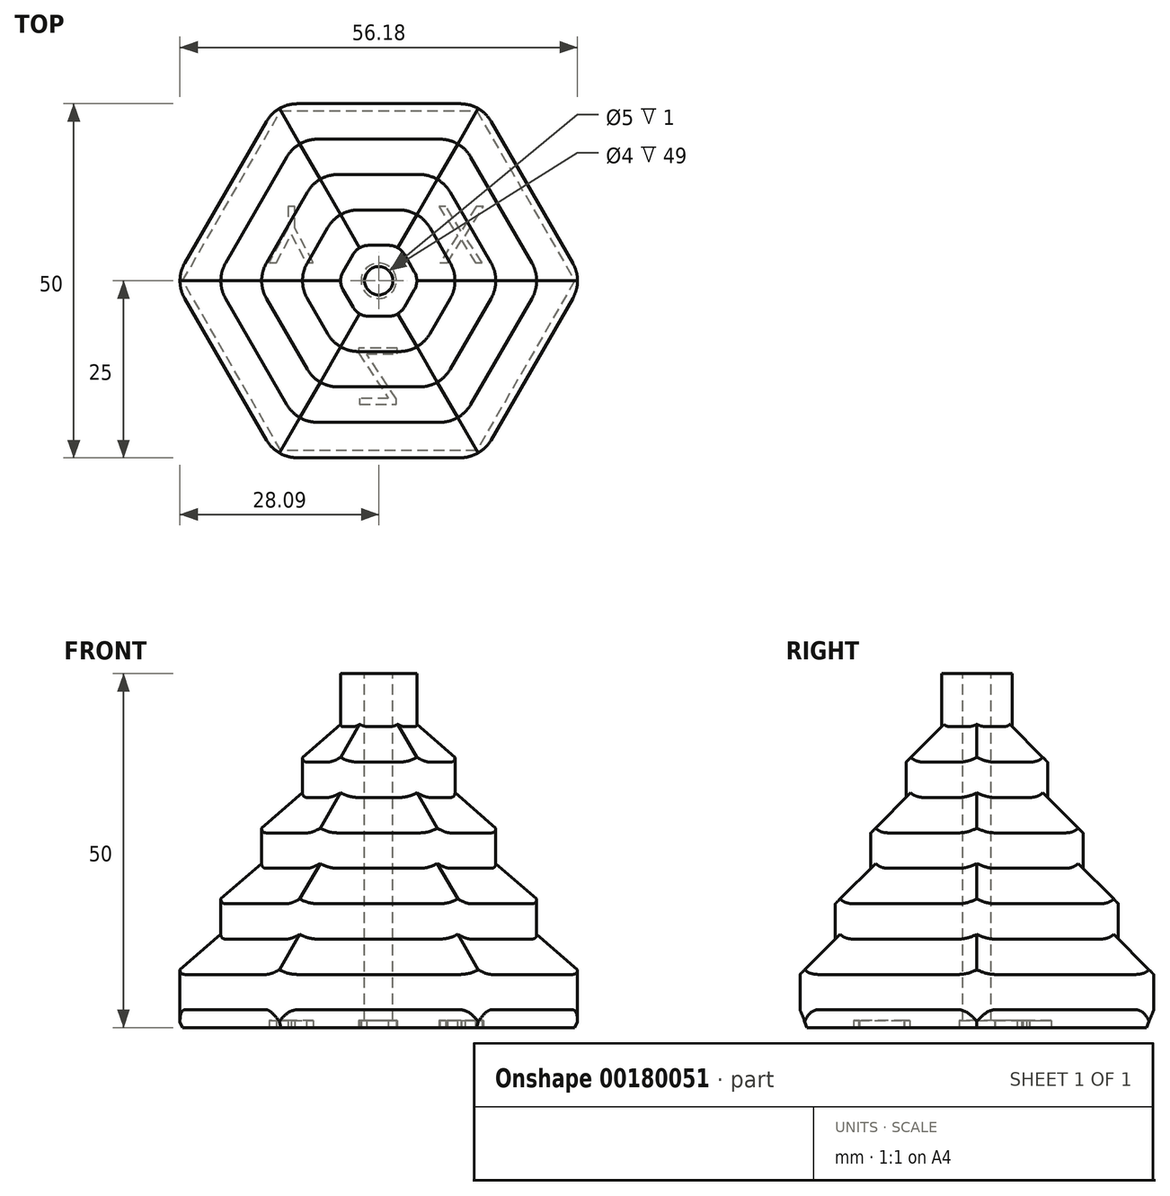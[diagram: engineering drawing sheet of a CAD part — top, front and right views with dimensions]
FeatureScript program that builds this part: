
annotation { "Feature Type Name" : "Feature", "Feature Type Description" : "" }
export const myFeature = defineFeature(function(context is Context, id is Id, definition is map)
    precondition{}
    {
        {
            var Q0;
            Q0=qCreatedBy(makeId("Top.planeOp"),FACE);
            var sketch = newSketch(context, id + "F0", { "sketchPlane" : qUnion([Q0])});
            skCircle(sketch, "E0.cCircle", {"center": v(0, 0) * mm, "radius": 25 * mm, "construction": true});
            skLineSegment(sketch, "E0.0", {"start": v(-14.43, 25) * mm, "end": v(14.43, 25) * mm});
            skLineSegment(sketch, "E0.1", {"start": v(14.43, 25) * mm, "end": v(28.87, 0) * mm});
            skLineSegment(sketch, "E0.2", {"start": v(28.87, 0) * mm, "end": v(14.43, -25) * mm});
            skLineSegment(sketch, "E0.3", {"start": v(14.43, -25) * mm, "end": v(-14.43, -25) * mm});
            skLineSegment(sketch, "E0.4", {"start": v(-14.43, -25) * mm, "end": v(-28.87, 0) * mm});
            skLineSegment(sketch, "E0.5", {"start": v(-28.87, 0) * mm, "end": v(-14.43, 25) * mm});
            skPoint(sketch, "E0.0.midPoint", {"position": v(0, 25) * mm});
            skSolve(sketch);
        }
        {
            var Q0;
            Q0 = qSketchRegion(id + "F0", true);
            extrude(context, id + "F1", {"entities" : qUnion([Q0]), "depth" : 10 * mm});
        }
        {
            var Q0;
            Q0=makeQuery(id+"F1.opExtrude","CAP_FACE",FACE,{"disambiguationData":[OSD([sQuery(id+"F0.wireOp",EDGE,"E0.0"),sQuery(id+"F0.wireOp",EDGE,"E0.1"),sQuery(id+"F0.wireOp",EDGE,"E0.2"),sQuery(id+"F0.wireOp",EDGE,"E0.3"),sQuery(id+"F0.wireOp",EDGE,"E0.4"),sQuery(id+"F0.wireOp",EDGE,"E0.5")])],"isStart":false});
            var sketch = newSketch(context, id + "F2", { "sketchPlane" : qUnion([Q0])});
            skCircle(sketch, "E1.cCircle", {"center": v(0, 0) * mm, "radius": 20 * mm, "construction": true});
            skLineSegment(sketch, "E1.0", {"start": v(-11.55, 20) * mm, "end": v(11.55, 20) * mm});
            skLineSegment(sketch, "E1.1", {"start": v(11.55, 20) * mm, "end": v(23.1, 0) * mm});
            skLineSegment(sketch, "E1.2", {"start": v(23.1, 0) * mm, "end": v(11.55, -20) * mm});
            skLineSegment(sketch, "E1.3", {"start": v(11.55, -20) * mm, "end": v(-11.55, -20) * mm});
            skLineSegment(sketch, "E1.4", {"start": v(-11.55, -20) * mm, "end": v(-23.1, 0) * mm});
            skLineSegment(sketch, "E1.5", {"start": v(-23.1, 0) * mm, "end": v(-11.55, 20) * mm});
            skPoint(sketch, "E1.0.midPoint", {"position": v(0, 20) * mm});
            skSolve(sketch);
        }
        {
            var Q0;
            Q0 = qSketchRegion(id + "F2", true);
            extrude(context, id + "F3", {"entities" : qUnion([Q0]), "operationType" : NewBodyOperationType.ADD, "depth" : 10 * mm});
        }
        {
            var Q0;
            Q0=makeQuery(id+"F3.opExtrude","CAP_FACE",FACE,{"disambiguationData":[OSD([sQuery(id+"F2.wireOp",EDGE,"E1.0"),sQuery(id+"F2.wireOp",EDGE,"E1.1"),sQuery(id+"F2.wireOp",EDGE,"E1.2"),sQuery(id+"F2.wireOp",EDGE,"E1.3"),sQuery(id+"F2.wireOp",EDGE,"E1.4"),sQuery(id+"F2.wireOp",EDGE,"E1.5")])],"isStart":false});
            var sketch = newSketch(context, id + "F4", { "sketchPlane" : qUnion([Q0])});
            skCircle(sketch, "E2.cCircle", {"center": v(0, 0) * mm, "radius": 15 * mm, "construction": true});
            skLineSegment(sketch, "E2.0", {"start": v(-8.66, 15) * mm, "end": v(8.66, 15) * mm});
            skLineSegment(sketch, "E2.1", {"start": v(8.66, 15) * mm, "end": v(17.32, 0) * mm});
            skLineSegment(sketch, "E2.2", {"start": v(17.32, 0) * mm, "end": v(8.66, -15) * mm});
            skLineSegment(sketch, "E2.3", {"start": v(8.66, -15) * mm, "end": v(-8.66, -15) * mm});
            skLineSegment(sketch, "E2.4", {"start": v(-8.66, -15) * mm, "end": v(-17.32, 0) * mm});
            skLineSegment(sketch, "E2.5", {"start": v(-17.32, 0) * mm, "end": v(-8.66, 15) * mm});
            skPoint(sketch, "E2.0.midPoint", {"position": v(0, 15) * mm});
            skSolve(sketch);
        }
        {
            var Q0;
            Q0 = qSketchRegion(id + "F4", true);
            extrude(context, id + "F5", {"entities" : qUnion([Q0]), "operationType" : NewBodyOperationType.ADD, "depth" : 10 * mm});
        }
        {
            var Q0;
            Q0=makeQuery(id+"F5.opExtrude","CAP_FACE",FACE,{"disambiguationData":[OSD([sQuery(id+"F4.wireOp",EDGE,"E2.0"),sQuery(id+"F4.wireOp",EDGE,"E2.1"),sQuery(id+"F4.wireOp",EDGE,"E2.2"),sQuery(id+"F4.wireOp",EDGE,"E2.3"),sQuery(id+"F4.wireOp",EDGE,"E2.4"),sQuery(id+"F4.wireOp",EDGE,"E2.5")])],"isStart":false});
            var sketch = newSketch(context, id + "F6", { "sketchPlane" : qUnion([Q0])});
            skCircle(sketch, "E3.cCircle", {"center": v(0, 0) * mm, "radius": 10 * mm, "construction": true});
            skLineSegment(sketch, "E3.0", {"start": v(-5.77, 10) * mm, "end": v(5.77, 10) * mm});
            skLineSegment(sketch, "E3.1", {"start": v(5.77, 10) * mm, "end": v(11.55, 0) * mm});
            skLineSegment(sketch, "E3.2", {"start": v(11.55, 0) * mm, "end": v(5.77, -10) * mm});
            skLineSegment(sketch, "E3.3", {"start": v(5.77, -10) * mm, "end": v(-5.77, -10) * mm});
            skLineSegment(sketch, "E3.4", {"start": v(-5.77, -10) * mm, "end": v(-11.55, 0) * mm});
            skLineSegment(sketch, "E3.5", {"start": v(-11.55, 0) * mm, "end": v(-5.77, 10) * mm});
            skPoint(sketch, "E3.0.midPoint", {"position": v(0, 10) * mm});
            skSolve(sketch);
        }
        {
            var Q0;
            Q0 = qSketchRegion(id + "F6", true);
            extrude(context, id + "F7", {"entities" : qUnion([Q0]), "operationType" : NewBodyOperationType.ADD, "depth" : 10 * mm});
        }
        {
            var Q0;
            Q0=makeQuery(id+"F7.opExtrude","CAP_FACE",FACE,{"disambiguationData":[OSD([sQuery(id+"F6.wireOp",EDGE,"E3.0"),sQuery(id+"F6.wireOp",EDGE,"E3.1"),sQuery(id+"F6.wireOp",EDGE,"E3.2"),sQuery(id+"F6.wireOp",EDGE,"E3.3"),sQuery(id+"F6.wireOp",EDGE,"E3.4"),sQuery(id+"F6.wireOp",EDGE,"E3.5")])],"isStart":false});
            var sketch = newSketch(context, id + "F8", { "sketchPlane" : qUnion([Q0])});
            skCircle(sketch, "E4.cCircle", {"center": v(0, 0) * mm, "radius": 5 * mm, "construction": true});
            skLineSegment(sketch, "E4.0", {"start": v(-2.89, 5) * mm, "end": v(2.89, 5) * mm});
            skLineSegment(sketch, "E4.1", {"start": v(2.89, 5) * mm, "end": v(5.77, 0) * mm});
            skLineSegment(sketch, "E4.2", {"start": v(5.77, 0) * mm, "end": v(2.89, -5) * mm});
            skLineSegment(sketch, "E4.3", {"start": v(2.89, -5) * mm, "end": v(-2.89, -5) * mm});
            skLineSegment(sketch, "E4.4", {"start": v(-2.89, -5) * mm, "end": v(-5.77, 0) * mm});
            skLineSegment(sketch, "E4.5", {"start": v(-5.77, 0) * mm, "end": v(-2.89, 5) * mm});
            skPoint(sketch, "E4.0.midPoint", {"position": v(0, 5) * mm});
            skSolve(sketch);
        }
        {
            var Q0;
            Q0 = qSketchRegion(id + "F8", true);
            extrude(context, id + "F9", {"entities" : qUnion([Q0]), "operationType" : NewBodyOperationType.ADD, "depth" : 10 * mm});
        }
        {
            var Q0;
            Q0=makeQuery(id+"F1.opExtrude","CAP_FACE",FACE,{"disambiguationData":[OSD([sQuery(id+"F0.wireOp",EDGE,"E0.0"),sQuery(id+"F0.wireOp",EDGE,"E0.1"),sQuery(id+"F0.wireOp",EDGE,"E0.2"),sQuery(id+"F0.wireOp",EDGE,"E0.3"),sQuery(id+"F0.wireOp",EDGE,"E0.4"),sQuery(id+"F0.wireOp",EDGE,"E0.5")])],"isStart":true});
            chamfer(context, id + "F10", {"entities" : qUnion([Q0]), "chamferType" : ChamferType.TWO_OFFSETS, "width1" : 1 * mm, "oppositeDirection" : false, "width2" : 2.5 * mm, "tangentPropagation" : true});
        }
        {
            var Q0;
            Q0=makeQuery(id+"F1.opExtrude","CAP_FACE",FACE,{"disambiguationData":[OSD([sQuery(id+"F0.wireOp",EDGE,"E0.0"),sQuery(id+"F0.wireOp",EDGE,"E0.1"),sQuery(id+"F0.wireOp",EDGE,"E0.2"),sQuery(id+"F0.wireOp",EDGE,"E0.3"),sQuery(id+"F0.wireOp",EDGE,"E0.4"),sQuery(id+"F0.wireOp",EDGE,"E0.5")])],"isStart":true});
            var sketch = newSketch(context, id + "F11", { "sketchPlane" : qUnion([Q0])});
            skText(sketch, "E5", { "text": "Z", "fontName": "OpenSans-Regular.ttf"});
            skText(sketch, "E6", { "text": "X", "fontName": "OpenSans-Regular.ttf"});
            skText(sketch, "E7", { "text": "Y", "fontName": "OpenSans-Regular.ttf"});
            skLineSegment(sketch, "E8", {"start": v(0, 24) * mm, "end": v(0, 0) * mm, "construction": true});
            skLineSegment(sketch, "E9", {"start": v(0, 0) * mm, "end": v(-20.78, -12) * mm, "construction": true});
            skLineSegment(sketch, "E10", {"start": v(0, 0) * mm, "end": v(20.78, -12) * mm, "construction": true});
            skCircle(sketch, "E11", {"center": v(0, 0) * mm, "radius": 2.5 * mm});
            const initialGuessF11  = {"E5": [-0.0033, 0.0095, 1, 0, 0.008], "E6": [0.00845, -0.0105, 1, 0, 0.008], "E7": [-0.01547, -0.0105, 1, 0, 0.008]};
            skSetInitialGuess(sketch, initialGuessF11);
            skSolve(sketch);
        }
        {
            var Q0;
            Q0 = qSketchRegion(id + "F11", true);
            extrude(context, id + "F12", {"entities" : qUnion([Q0]), "operationType" : NewBodyOperationType.REMOVE, "oppositeDirection" : true, "depth" : 1 * mm});
        }
        {
            var Q0;
            Q0=makeQuery(id+"F9.opExtrude","CAP_FACE",FACE,{"disambiguationData":[OSD([sQuery(id+"F8.wireOp",EDGE,"E4.0"),sQuery(id+"F8.wireOp",EDGE,"E4.1"),sQuery(id+"F8.wireOp",EDGE,"E4.2"),sQuery(id+"F8.wireOp",EDGE,"E4.3"),sQuery(id+"F8.wireOp",EDGE,"E4.4"),sQuery(id+"F8.wireOp",EDGE,"E4.5")])],"isStart":false});
            var sketch = newSketch(context, id + "F13", { "sketchPlane" : qUnion([Q0])});
            skCircle(sketch, "E12", {"center": v(0, 0) * mm, "radius": 2 * mm});
            skSolve(sketch);
        }
        {
            var Q0;
            Q0 = qSketchRegion(id + "F13", true);
            extrude(context, id + "F14", {"entities" : qUnion([Q0]), "operationType" : NewBodyOperationType.REMOVE, "endBound" : BoundingType.THROUGH_ALL, "oppositeDirection" : true, "depth" : 25 * mm});
        }
        {
            var Q0;
            Q0=makeQuery(id+"F1.opExtrude","CAP_FACE",FACE,{"disambiguationData":[OSD([sQuery(id+"F0.wireOp",EDGE,"E0.0"),sQuery(id+"F0.wireOp",EDGE,"E0.1"),sQuery(id+"F0.wireOp",EDGE,"E0.2"),sQuery(id+"F0.wireOp",EDGE,"E0.3"),sQuery(id+"F0.wireOp",EDGE,"E0.4"),sQuery(id+"F0.wireOp",EDGE,"E0.5")])],"isStart":false});
            var Q1;
            Q1=makeQuery(id+"F3.opExtrude","CAP_FACE",FACE,{"disambiguationData":[OSD([sQuery(id+"F2.wireOp",EDGE,"E1.0"),sQuery(id+"F2.wireOp",EDGE,"E1.1"),sQuery(id+"F2.wireOp",EDGE,"E1.2"),sQuery(id+"F2.wireOp",EDGE,"E1.3"),sQuery(id+"F2.wireOp",EDGE,"E1.4"),sQuery(id+"F2.wireOp",EDGE,"E1.5")])],"isStart":false});
            var Q2;
            Q2=makeQuery(id+"F5.opExtrude","CAP_FACE",FACE,{"disambiguationData":[OSD([sQuery(id+"F4.wireOp",EDGE,"E2.0"),sQuery(id+"F4.wireOp",EDGE,"E2.1"),sQuery(id+"F4.wireOp",EDGE,"E2.2"),sQuery(id+"F4.wireOp",EDGE,"E2.3"),sQuery(id+"F4.wireOp",EDGE,"E2.4"),sQuery(id+"F4.wireOp",EDGE,"E2.5")])],"isStart":false});
            var Q3;
            Q3=makeQuery(id+"F7.opExtrude","CAP_FACE",FACE,{"disambiguationData":[OSD([sQuery(id+"F6.wireOp",EDGE,"E3.0"),sQuery(id+"F6.wireOp",EDGE,"E3.1"),sQuery(id+"F6.wireOp",EDGE,"E3.2"),sQuery(id+"F6.wireOp",EDGE,"E3.3"),sQuery(id+"F6.wireOp",EDGE,"E3.4"),sQuery(id+"F6.wireOp",EDGE,"E3.5")])],"isStart":false});
            chamfer(context, id + "F15", {"entities" : qUnion([Q0, Q1, Q2, Q3]), "width" : 2.5 * mm, "tangentPropagation" : true});
        }
        {
            var Q0;
            Q0=makeQuery(id+"F1.opExtrude","SWEPT_EDGE",EDGE,{"disambiguationData":[OSD([sQuery(id+"F0.wireOp",EDGE,"E0.2"),sQuery(id+"F0.wireOp",EDGE,"E0.3")])]});
            var Q1;
            Q1=makeQuery(id+"F1.opExtrude","SWEPT_EDGE",EDGE,{"disambiguationData":[OSD([sQuery(id+"F0.wireOp",EDGE,"E0.1"),sQuery(id+"F0.wireOp",EDGE,"E0.2")])]});
            var Q2;
            Q2=makeQuery(id+"F1.opExtrude","SWEPT_EDGE",EDGE,{"disambiguationData":[OSD([sQuery(id+"F0.wireOp",EDGE,"E0.0"),sQuery(id+"F0.wireOp",EDGE,"E0.1")])]});
            var Q3;
            Q3=makeQuery(id+"F1.opExtrude","SWEPT_EDGE",EDGE,{"disambiguationData":[OSD([sQuery(id+"F0.wireOp",EDGE,"E0.0"),sQuery(id+"F0.wireOp",EDGE,"E0.5")])]});
            var Q4;
            Q4=makeQuery(id+"F1.opExtrude","SWEPT_EDGE",EDGE,{"disambiguationData":[OSD([sQuery(id+"F0.wireOp",EDGE,"E0.4"),sQuery(id+"F0.wireOp",EDGE,"E0.5")])]});
            var Q5;
            Q5=makeQuery(id+"F1.opExtrude","SWEPT_EDGE",EDGE,{"disambiguationData":[OSD([sQuery(id+"F0.wireOp",EDGE,"E0.3"),sQuery(id+"F0.wireOp",EDGE,"E0.4")])]});
            var Q6;
            Q6=makeQuery(id+"F3.opExtrude","SWEPT_EDGE",EDGE,{"disambiguationData":[OSD([sQuery(id+"F2.wireOp",EDGE,"E1.3"),sQuery(id+"F2.wireOp",EDGE,"E1.4")])]});
            var Q7;
            Q7=makeQuery(id+"F3.opExtrude","SWEPT_EDGE",EDGE,{"disambiguationData":[OSD([sQuery(id+"F2.wireOp",EDGE,"E1.2"),sQuery(id+"F2.wireOp",EDGE,"E1.3")])]});
            var Q8;
            Q8=makeQuery(id+"F3.opExtrude","SWEPT_EDGE",EDGE,{"disambiguationData":[OSD([sQuery(id+"F2.wireOp",EDGE,"E1.1"),sQuery(id+"F2.wireOp",EDGE,"E1.2")])]});
            var Q9;
            Q9=makeQuery(id+"F3.opExtrude","SWEPT_EDGE",EDGE,{"disambiguationData":[OSD([sQuery(id+"F2.wireOp",EDGE,"E1.0"),sQuery(id+"F2.wireOp",EDGE,"E1.1")])]});
            var Q10;
            Q10=makeQuery(id+"F3.opExtrude","SWEPT_EDGE",EDGE,{"disambiguationData":[OSD([sQuery(id+"F2.wireOp",EDGE,"E1.0"),sQuery(id+"F2.wireOp",EDGE,"E1.5")])]});
            var Q11;
            Q11=makeQuery(id+"F3.opExtrude","SWEPT_EDGE",EDGE,{"disambiguationData":[OSD([sQuery(id+"F2.wireOp",EDGE,"E1.4"),sQuery(id+"F2.wireOp",EDGE,"E1.5")])]});
            var Q12;
            Q12=makeQuery(id+"F5.opExtrude","SWEPT_EDGE",EDGE,{"disambiguationData":[OSD([sQuery(id+"F4.wireOp",EDGE,"E2.2"),sQuery(id+"F4.wireOp",EDGE,"E2.3")])]});
            var Q13;
            Q13=makeQuery(id+"F5.opExtrude","SWEPT_EDGE",EDGE,{"disambiguationData":[OSD([sQuery(id+"F4.wireOp",EDGE,"E2.3"),sQuery(id+"F4.wireOp",EDGE,"E2.4")])]});
            var Q14;
            Q14=makeQuery(id+"F5.opExtrude","SWEPT_EDGE",EDGE,{"disambiguationData":[OSD([sQuery(id+"F4.wireOp",EDGE,"E2.1"),sQuery(id+"F4.wireOp",EDGE,"E2.2")])]});
            var Q15;
            Q15=makeQuery(id+"F5.opExtrude","SWEPT_EDGE",EDGE,{"disambiguationData":[OSD([sQuery(id+"F4.wireOp",EDGE,"E2.0"),sQuery(id+"F4.wireOp",EDGE,"E2.1")])]});
            var Q16;
            Q16=makeQuery(id+"F5.opExtrude","SWEPT_EDGE",EDGE,{"disambiguationData":[OSD([sQuery(id+"F4.wireOp",EDGE,"E2.0"),sQuery(id+"F4.wireOp",EDGE,"E2.5")])]});
            var Q17;
            Q17=makeQuery(id+"F5.opExtrude","SWEPT_EDGE",EDGE,{"disambiguationData":[OSD([sQuery(id+"F4.wireOp",EDGE,"E2.4"),sQuery(id+"F4.wireOp",EDGE,"E2.5")])]});
            var Q18;
            Q18=makeQuery(id+"F7.opExtrude","SWEPT_EDGE",EDGE,{"disambiguationData":[OSD([sQuery(id+"F6.wireOp",EDGE,"E3.4"),sQuery(id+"F6.wireOp",EDGE,"E3.5")])]});
            var Q19;
            Q19=makeQuery(id+"F7.opExtrude","SWEPT_EDGE",EDGE,{"disambiguationData":[OSD([sQuery(id+"F6.wireOp",EDGE,"E3.0"),sQuery(id+"F6.wireOp",EDGE,"E3.5")])]});
            var Q20;
            Q20=makeQuery(id+"F7.opExtrude","SWEPT_EDGE",EDGE,{"disambiguationData":[OSD([sQuery(id+"F6.wireOp",EDGE,"E3.0"),sQuery(id+"F6.wireOp",EDGE,"E3.1")])]});
            var Q21;
            Q21=makeQuery(id+"F7.opExtrude","SWEPT_EDGE",EDGE,{"disambiguationData":[OSD([sQuery(id+"F6.wireOp",EDGE,"E3.1"),sQuery(id+"F6.wireOp",EDGE,"E3.2")])]});
            var Q22;
            Q22=makeQuery(id+"F7.opExtrude","SWEPT_EDGE",EDGE,{"disambiguationData":[OSD([sQuery(id+"F6.wireOp",EDGE,"E3.2"),sQuery(id+"F6.wireOp",EDGE,"E3.3")])]});
            var Q23;
            Q23=makeQuery(id+"F7.opExtrude","SWEPT_EDGE",EDGE,{"disambiguationData":[OSD([sQuery(id+"F6.wireOp",EDGE,"E3.3"),sQuery(id+"F6.wireOp",EDGE,"E3.4")])]});
            fillet(context, id + "F16", {"entities" : qUnion([Q0, Q1, Q2, Q3, Q4, Q5, Q6, Q7, Q8, Q9, Q10, Q11, Q12, Q13, Q14, Q15, Q16, Q17, Q18, Q19, Q20, Q21, Q22, Q23]), "radius" : 5 * mm, "tangentPropagation" : true, "allowEdgeOverflow" : false});
        }
        {
            var Q0;
            Q0=makeQuery(id+"F9.opExtrude","SWEPT_EDGE",EDGE,{"disambiguationData":[OSD([sQuery(id+"F8.wireOp",EDGE,"E4.2"),sQuery(id+"F8.wireOp",EDGE,"E4.3")])]});
            var Q1;
            Q1=makeQuery(id+"F9.opExtrude","SWEPT_EDGE",EDGE,{"disambiguationData":[OSD([sQuery(id+"F8.wireOp",EDGE,"E4.1"),sQuery(id+"F8.wireOp",EDGE,"E4.2")])]});
            var Q2;
            Q2=makeQuery(id+"F9.opExtrude","SWEPT_EDGE",EDGE,{"disambiguationData":[OSD([sQuery(id+"F8.wireOp",EDGE,"E4.0"),sQuery(id+"F8.wireOp",EDGE,"E4.1")])]});
            var Q3;
            Q3=makeQuery(id+"F9.opExtrude","SWEPT_EDGE",EDGE,{"disambiguationData":[OSD([sQuery(id+"F8.wireOp",EDGE,"E4.0"),sQuery(id+"F8.wireOp",EDGE,"E4.5")])]});
            var Q4;
            Q4=makeQuery(id+"F9.opExtrude","SWEPT_EDGE",EDGE,{"disambiguationData":[OSD([sQuery(id+"F8.wireOp",EDGE,"E4.4"),sQuery(id+"F8.wireOp",EDGE,"E4.5")])]});
            var Q5;
            Q5=makeQuery(id+"F9.opExtrude","SWEPT_EDGE",EDGE,{"disambiguationData":[OSD([sQuery(id+"F8.wireOp",EDGE,"E4.3"),sQuery(id+"F8.wireOp",EDGE,"E4.4")])]});
            fillet(context, id + "F17", {"entities" : qUnion([Q0, Q1, Q2, Q3, Q4, Q5]), "radius" : 2.5 * mm, "tangentPropagation" : true, "allowEdgeOverflow" : false});
        }
    });
